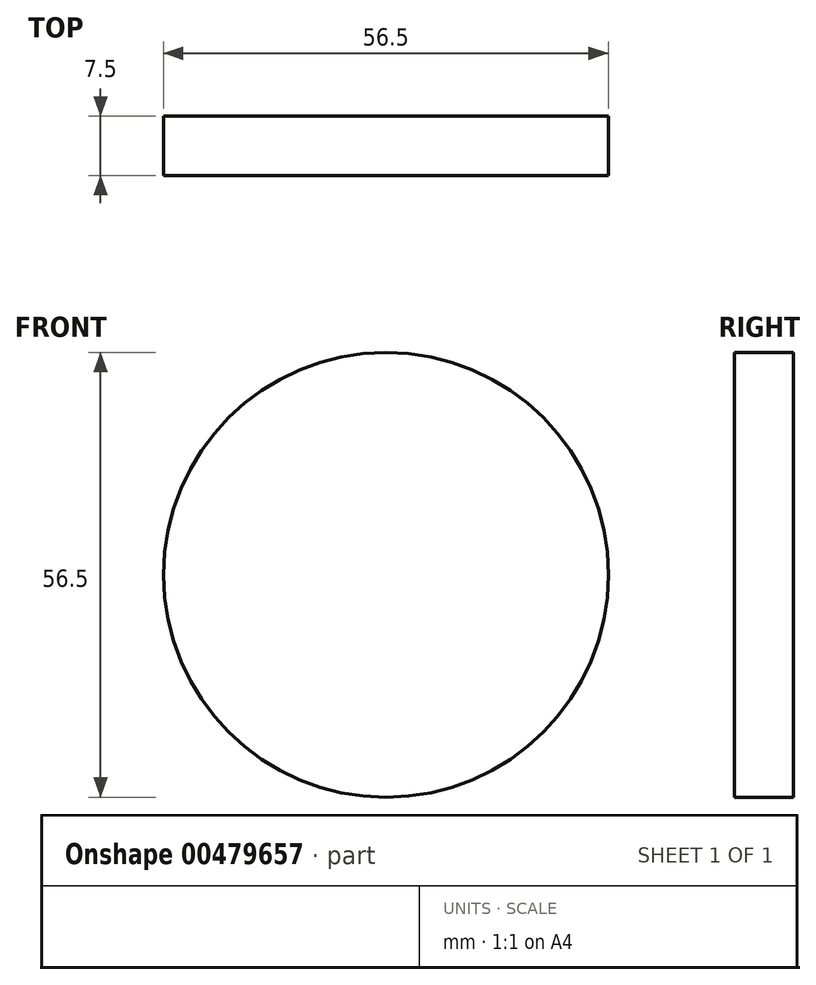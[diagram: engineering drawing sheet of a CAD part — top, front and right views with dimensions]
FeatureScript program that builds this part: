
annotation { "Feature Type Name" : "Feature", "Feature Type Description" : "" }
export const myFeature = defineFeature(function(context is Context, id is Id, definition is map)
    precondition{}
    {
        {
            var Q0;
            Q0=qCreatedBy(makeId("Front.planeOp"),FACE);
            var sketch = newSketch(context, id + "F0", { "sketchPlane" : qUnion([Q0])});
            skCircle(sketch, "E0", {"center": v(0, 0) * mm, "radius": 28.25 * mm});
            skSolve(sketch);
        }
        {
            var Q0;
            Q0=makeQuery(id+"F0.imprint","IMPRINT",FACE,{"disambiguationData":[TD([[makeQuery(id+"F0.imprint","IMPRINT",EDGE,{"derivedFrom":sQuery(id+"F0.wireOp",EDGE,"E0")}),1.0]])]});
            extrude(context, id + "F1", {"entities" : qUnion([Q0]), "depth" : 7.5 * mm});
        }
    });
